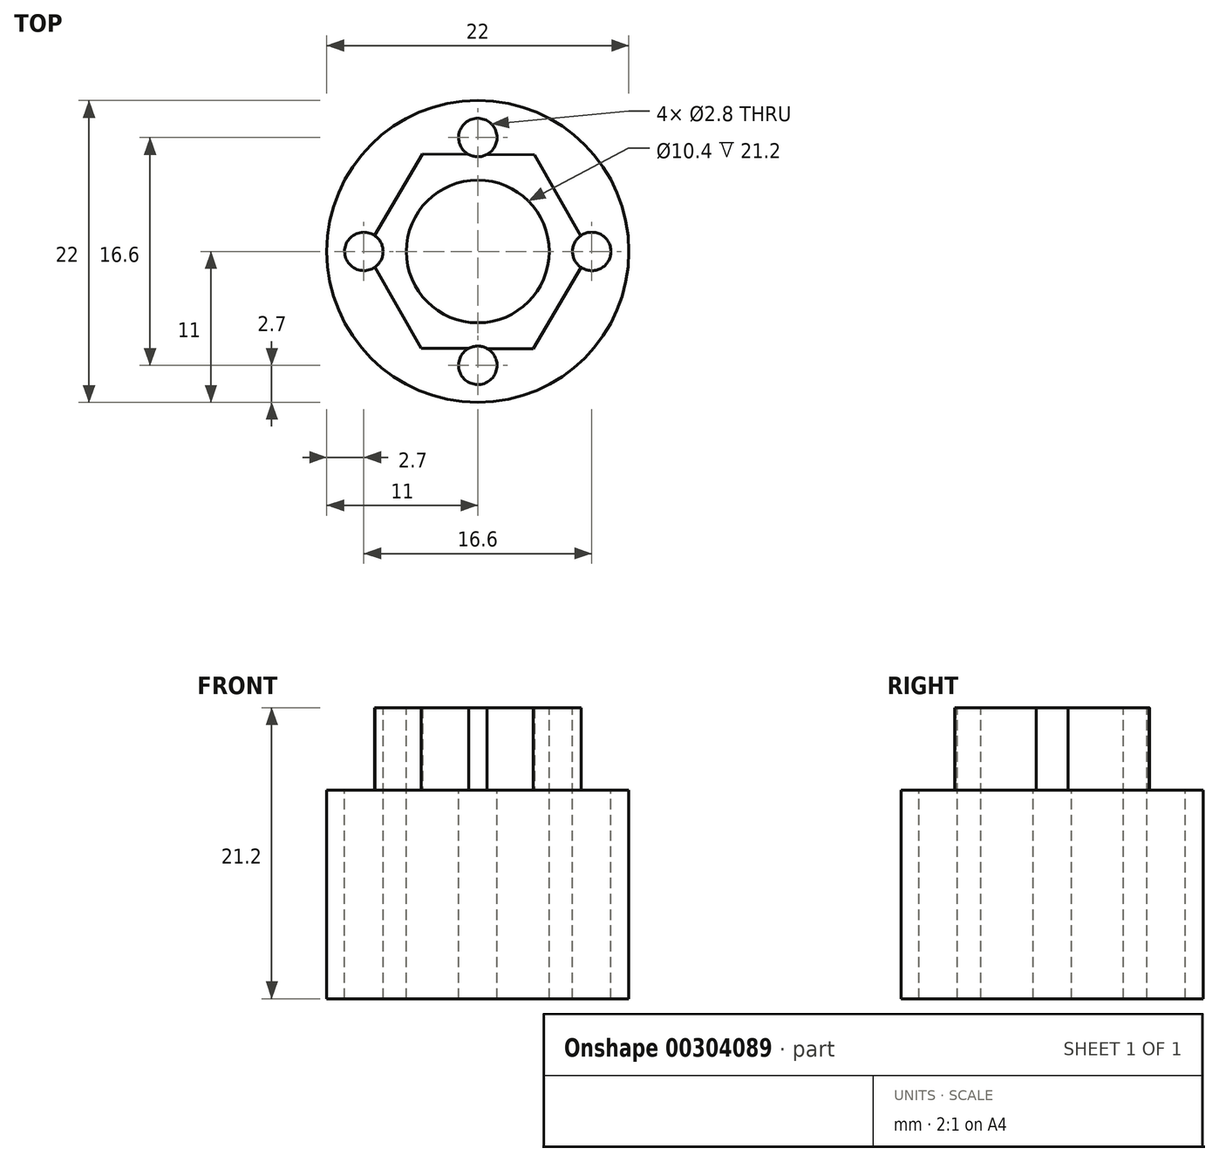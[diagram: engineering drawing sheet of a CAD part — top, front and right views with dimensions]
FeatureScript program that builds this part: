
annotation { "Feature Type Name" : "Feature", "Feature Type Description" : "" }
export const myFeature = defineFeature(function(context is Context, id is Id, definition is map)
    precondition{}
    {
        {
            var Q0;
            Q0=qCreatedBy(makeId("Top.planeOp"),FACE);
            var sketch = newSketch(context, id + "F0", { "sketchPlane" : qUnion([Q0])});
            skCircle(sketch, "E0", {"center": v(0, 0) * mm, "radius": 11 * mm});
            skSolve(sketch);
        }
        {
            var Q0;
            Q0=makeQuery(id+"F0.imprint","IMPRINT",FACE,{"disambiguationData":[TD([[makeQuery(id+"F0.imprint","IMPRINT",EDGE,{"derivedFrom":sQuery(id+"F0.wireOp",EDGE,"E0")}),1.0]])]});
            extrude(context, id + "F1", {"entities" : qUnion([Q0]), "depth" : 15.2 * mm});
        }
        {
            var Q0;
            Q0=makeQuery(id+"F1.opExtrude","CAP_FACE",FACE,{"disambiguationData":[OSD([sQuery(id+"F0.wireOp",EDGE,"E0")])],"isStart":false});
            var sketch = newSketch(context, id + "F2", { "sketchPlane" : qUnion([Q0])});
            skCircle(sketch, "E1", {"center": v(0, 0) * mm, "radius": 5.1 * mm});
            skSolve(sketch);
        }
        {
            var Q0;
            Q0=makeQuery(id+"F2.imprint","IMPRINT",FACE,{"disambiguationData":[TD([[makeQuery(id+"F2.imprint","IMPRINT",EDGE,{"derivedFrom":sQuery(id+"F2.wireOp",EDGE,"E1")}),1.0]])]});
            extrude(context, id + "F3", {"entities" : qUnion([Q0]), "operationType" : NewBodyOperationType.REMOVE, "oppositeDirection" : true, "depth" : 50 * mm, "hasSecondDirection" : true, "secondDirectionOppositeDirection" : false, "secondDirectionDepth" : 50 * mm});
        }
        {
            var Q0;
            Q0=makeQuery(id+"F1.opExtrude","CAP_FACE",FACE,{"disambiguationData":[OSD([sQuery(id+"F0.wireOp",EDGE,"E0")])],"isStart":false});
            var sketch = newSketch(context, id + "F4", { "sketchPlane" : qUnion([Q0])});
            skLineSegment(sketch, "E2", {"start": v(0, 11) * mm, "end": v(0, -11) * mm, "construction": true});
            skLineSegment(sketch, "E3", {"start": v(11, 0) * mm, "end": v(-11, 0) * mm, "construction": true});
            skCircle(sketch, "E4", {"center": v(-8.3, 0) * mm, "radius": 1.4 * mm});
            skCircle(sketch, "E5", {"center": v(8.3, 0) * mm, "radius": 1.4 * mm});
            skCircle(sketch, "E6", {"center": v(0, 8.3) * mm, "radius": 1.4 * mm});
            skCircle(sketch, "E7", {"center": v(0, -8.3) * mm, "radius": 1.4 * mm});
            skSolve(sketch);
        }
        {
            var Q0;
            Q0=makeQuery(id+"F4.imprint","IMPRINT",FACE,{"disambiguationData":[TD([[makeQuery(id+"F4.imprint","IMPRINT",EDGE,{"derivedFrom":sQuery(id+"F4.wireOp",EDGE,"E7")}),1.0]])]});
            var Q1;
            Q1=makeQuery(id+"F4.imprint","IMPRINT",FACE,{"disambiguationData":[TD([[makeQuery(id+"F4.imprint","IMPRINT",EDGE,{"derivedFrom":sQuery(id+"F4.wireOp",EDGE,"E4")}),1.0]])]});
            var Q2;
            Q2=makeQuery(id+"F4.imprint","IMPRINT",FACE,{"disambiguationData":[TD([[makeQuery(id+"F4.imprint","IMPRINT",EDGE,{"derivedFrom":sQuery(id+"F4.wireOp",EDGE,"E6")}),1.0]])]});
            var Q3;
            Q3=makeQuery(id+"F4.imprint","IMPRINT",FACE,{"disambiguationData":[TD([[makeQuery(id+"F4.imprint","IMPRINT",EDGE,{"derivedFrom":sQuery(id+"F4.wireOp",EDGE,"E5")}),1.0]])]});
            var Q4;
            Q4=sQuery(id+"F4.wireOp",EDGE,"E4");
            extrude(context, id + "F5", {"entities" : qUnion([Q0, Q1, Q2, Q3]), "operationType" : NewBodyOperationType.REMOVE, "surfaceEntities" : qUnion([Q4]), "oppositeDirection" : true, "depth" : 25 * mm});
        }
        {
            var Q0;
            Q0=makeQuery(id+"F1.opExtrude","CAP_FACE",FACE,{"disambiguationData":[OSD([sQuery(id+"F0.wireOp",EDGE,"E0")])],"isStart":false});
            var sketch = newSketch(context, id + "F6", { "sketchPlane" : qUnion([Q0])});
            skCircle(sketch, "E8.cCircle", {"center": v(0, 0) * mm, "radius": 7.08 * mm, "construction": true});
            skLineSegment(sketch, "E8.0", {"start": v(8.17, -0.05) * mm, "end": v(4.04, -7.1) * mm});
            skLineSegment(sketch, "E8.1", {"start": v(4.04, -7.1) * mm, "end": v(-4.13, -7.05) * mm});
            skLineSegment(sketch, "E8.2", {"start": v(-4.13, -7.05) * mm, "end": v(-8.17, 0.05) * mm});
            skLineSegment(sketch, "E8.3", {"start": v(-8.17, 0.05) * mm, "end": v(-4.04, 7.1) * mm});
            skLineSegment(sketch, "E8.4", {"start": v(-4.04, 7.1) * mm, "end": v(4.13, 7.05) * mm});
            skLineSegment(sketch, "E8.5", {"start": v(4.13, 7.05) * mm, "end": v(8.17, -0.05) * mm});
            skPoint(sketch, "E8.0.midPoint", {"position": v(6.1, -3.58) * mm});
            skSolve(sketch);
        }
        {
            var Q0;
            Q0 = qSketchRegion(id + "F6", true);
            extrude(context, id + "F7", {"entities" : qUnion([Q0]), "operationType" : NewBodyOperationType.ADD, "depth" : 6 * mm});
        }
        {
            var Q0;
            Q0=makeQuery(id+"F7.opExtrude","CAP_FACE",FACE,{"disambiguationData":[OSD([sQuery(id+"F6.wireOp",EDGE,"E8.0"),sQuery(id+"F6.wireOp",EDGE,"E8.1"),sQuery(id+"F6.wireOp",EDGE,"E8.2"),sQuery(id+"F6.wireOp",EDGE,"E8.3"),sQuery(id+"F6.wireOp",EDGE,"E8.4"),sQuery(id+"F6.wireOp",EDGE,"E8.5")])],"isStart":false});
            var sketch = newSketch(context, id + "F8", { "sketchPlane" : qUnion([Q0])});
            skCircle(sketch, "E9", {"center": v(0, 0) * mm, "radius": 5.2 * mm});
            skSolve(sketch);
        }
        {
            var Q0;
            Q0=makeQuery(id+"F8.imprint","IMPRINT",FACE,{"disambiguationData":[TD([[makeQuery(id+"F8.imprint","IMPRINT",EDGE,{"derivedFrom":sQuery(id+"F8.wireOp",EDGE,"E9")}),1.0]])]});
            var Q1;
            Q1=sQuery(id+"F8.wireOp",EDGE,"E9");
            extrude(context, id + "F9", {"entities" : qUnion([Q0]), "operationType" : NewBodyOperationType.REMOVE, "surfaceEntities" : qUnion([Q1]), "oppositeDirection" : true, "depth" : 50 * mm});
        }
        {
            var Q0;
            Q0 = qSketchRegion(id + "F4", true);
            extrude(context, id + "F10", {"entities" : qUnion([Q0]), "operationType" : NewBodyOperationType.REMOVE, "depth" : 25 * mm});
        }
    });
